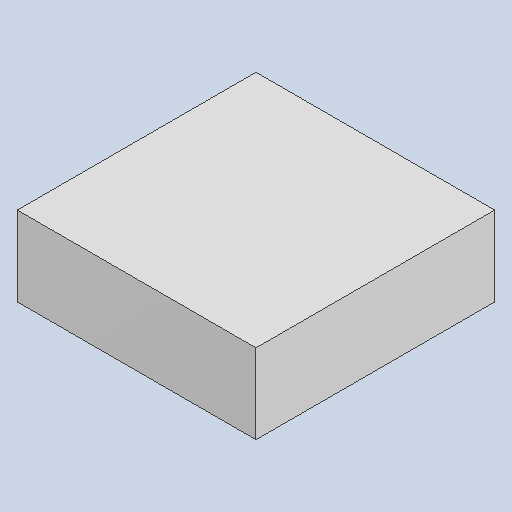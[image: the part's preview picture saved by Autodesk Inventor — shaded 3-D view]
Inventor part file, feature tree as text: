
AUTODESK INVENTOR PART (.ipt)
format: ipt  version: 2023.4 (Build 274418000, 418)  size: 79,872 bytes
history: native  units: mm
features: extrude x1
ambient origin geometry x8: Origin, YZ Plane, XZ Plane, XY Plane, X Axis, Y Axis, Z Axis, Center Point
bodies: Solid1 (feature_tree)
feature tree (1):
  extrude  "Extruded_43"  [1 undecoded]
note: 1 required parameter value undecoded (feature->parameter linkage not recoverable at this tier; creation-order binding heuristic only, values carry confidence <= 0.55)
